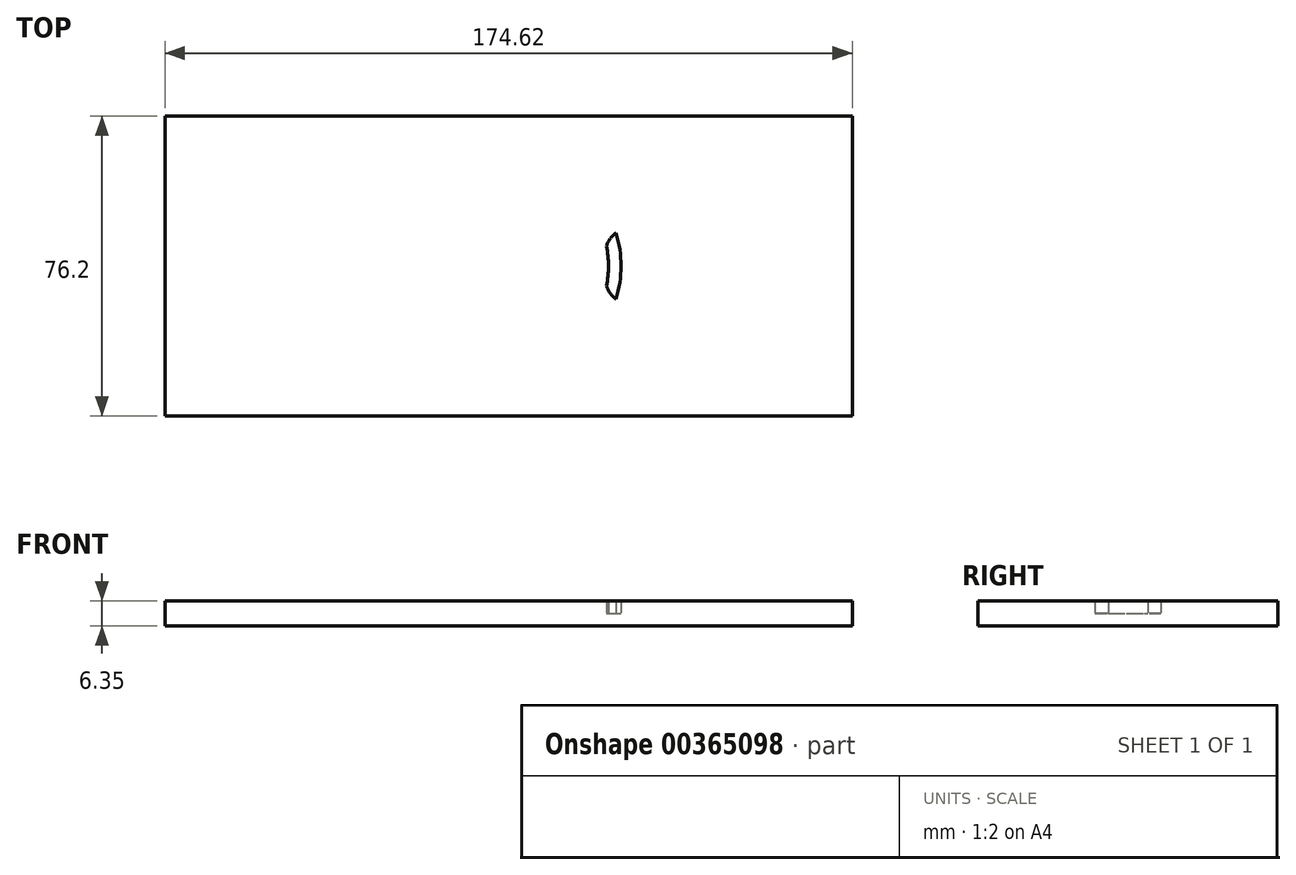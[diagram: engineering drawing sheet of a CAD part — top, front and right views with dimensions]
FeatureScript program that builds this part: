
annotation { "Feature Type Name" : "Feature", "Feature Type Description" : "" }
export const myFeature = defineFeature(function(context is Context, id is Id, definition is map)
    precondition{}
    {
        {
            var Q0;
            Q0=qCreatedBy(makeId("Top.planeOp"),FACE);
            var sketch = newSketch(context, id + "F0", { "sketchPlane" : qUnion([Q0])});
            skCircle(sketch, "E0", {"center": v(0, 0) * mm, "radius": 28.58 * mm});
            skLineSegment(sketch, "E1.bottom", {"start": v(87.31, -38.1) * mm, "end": v(-87.31, -38.1) * mm});
            skLineSegment(sketch, "E1.top", {"start": v(87.31, 38.1) * mm, "end": v(-87.31, 38.1) * mm});
            skLineSegment(sketch, "E1.left", {"start": v(87.31, -38.1) * mm, "end": v(87.31, 38.1) * mm});
            skLineSegment(sketch, "E1.right", {"start": v(-87.31, -38.1) * mm, "end": v(-87.31, 38.1) * mm});
            skLineSegment(sketch, "E2.bottom", {"start": v(25.4, -25.4) * mm, "end": v(-25.4, -25.4) * mm});
            skLineSegment(sketch, "E2.top", {"start": v(25.4, 25.4) * mm, "end": v(-25.4, 25.4) * mm});
            skLineSegment(sketch, "E2.left", {"start": v(25.4, -25.4) * mm, "end": v(25.4, 25.4) * mm});
            skLineSegment(sketch, "E2.right", {"start": v(-25.4, -25.4) * mm, "end": v(-25.4, 25.4) * mm});
            skCircle(sketch, "E3", {"center": v(-25.4, 25.4) * mm, "radius": 1.59 * mm});
            skCircle(sketch, "E4", {"center": v(-25.4, -25.4) * mm, "radius": 1.59 * mm});
            skCircle(sketch, "E5", {"center": v(25.4, -25.4) * mm, "radius": 1.59 * mm});
            skCircle(sketch, "E6", {"center": v(25.4, 25.4) * mm, "radius": 1.59 * mm});
            skCircle(sketch, "E7.0", {"center": v(0, 0) * mm, "radius": 25.4 * mm});
            skSolve(sketch);
        }
        {
            var Q0;
            Q0=makeQuery(id+"F0.imprint","IMPRINT",FACE,{"disambiguationData":[TD([[makeQuery(id+"F0.imprint","IMPRINT",EDGE,{"derivedFrom":sQuery(id+"F0.wireOp",EDGE,"E1.bottom")}),-1.0]])]});
            var Q1;
            {var subQ0=sQuery(id+"F0.wireOp",EDGE,"E2.left");var subQ1=sQuery(id+"F0.wireOp",EDGE,"E0");var subQ2=makeQuery(id+"F0.imprint","INTERSECT",VERTEX,{"derivedFrom":[subQ1,subQ0]});Q1=makeQuery(id+"F0.imprint","IMPRINT",FACE,{"disambiguationData":[TD([[makeQuery(id+"F0.imprint","IMPRINT",EDGE,{"disambiguationData":[TD([[subQ2,1.0]])],"derivedFrom":subQ1}),-1.0]])]});}
            var Q2;
            {var subQ0=sQuery(id+"F0.wireOp",EDGE,"E2.right");var subQ1=sQuery(id+"F0.wireOp",EDGE,"E0");var subQ2=makeQuery(id+"F0.imprint","INTERSECT",VERTEX,{"derivedFrom":[subQ1,subQ0]});Q2=makeQuery(id+"F0.imprint","IMPRINT",FACE,{"disambiguationData":[TD([[makeQuery(id+"F0.imprint","IMPRINT",EDGE,{"disambiguationData":[TD([[subQ2,-1.0]])],"derivedFrom":subQ1}),-1.0]])]});}
            var Q3;
            {var subQ0=sQuery(id+"F0.wireOp",EDGE,"E2.top");var subQ1=sQuery(id+"F0.wireOp",EDGE,"E0");var subQ2=makeQuery(id+"F0.imprint","INTERSECT",VERTEX,{"derivedFrom":[subQ1,subQ0]});Q3=makeQuery(id+"F0.imprint","IMPRINT",FACE,{"disambiguationData":[TD([[makeQuery(id+"F0.imprint","IMPRINT",EDGE,{"disambiguationData":[TD([[subQ2,1.0]])],"derivedFrom":subQ1}),-1.0]])]});}
            var Q4;
            {var subQ0=sQuery(id+"F0.wireOp",EDGE,"E2.top");var subQ1=sQuery(id+"F0.wireOp",EDGE,"E0");var subQ2=makeQuery(id+"F0.imprint","INTERSECT",VERTEX,{"derivedFrom":[subQ1,subQ0]});Q4=makeQuery(id+"F0.imprint","IMPRINT",FACE,{"disambiguationData":[TD([[makeQuery(id+"F0.imprint","IMPRINT",EDGE,{"disambiguationData":[TD([[subQ2,-1.0]])],"derivedFrom":subQ1}),-1.0]])]});}
            var Q5;
            {var subQ0=sQuery(id+"F0.wireOp",EDGE,"E7.0");var subQ1=makeQuery(id+"F0.imprint","INTERSECT",VERTEX,{"derivedFrom":[sQuery(id+"F0.wireOp",EDGE,"E2.top"),subQ0]});Q5=makeQuery(id+"F0.imprint","IMPRINT",FACE,{"disambiguationData":[TD([[makeQuery(id+"F0.imprint","IMPRINT",EDGE,{"disambiguationData":[TD([[subQ1,1.0]])],"derivedFrom":subQ0}),1.0]])]});}
            extrude(context, id + "F1", {"entities" : qUnion([Q0, Q1, Q2, Q3, Q4, Q5]), "depth" : 6.35 * mm});
        }
        {
            var Q0;
            Q0=qCreatedBy(makeId("Top.planeOp"),FACE);
            var sketch = newSketch(context, id + "F2", { "sketchPlane" : qUnion([Q0])});
            skLineSegment(sketch, "E8.0", {"start": v(87.31, -38.1) * mm, "end": v(-87.31, -38.1) * mm});
            skLineSegment(sketch, "E9.0", {"start": v(-87.31, -38.1) * mm, "end": v(-87.31, 38.1) * mm});
            skLineSegment(sketch, "E10.0", {"start": v(87.31, 38.1) * mm, "end": v(-87.31, 38.1) * mm});
            skLineSegment(sketch, "E11.0.0", {"start": v(87.31, -38.1) * mm, "end": v(87.31, 38.1) * mm});
            skLineSegment(sketch, "E11.0.2", {"start": v(-87.31, 38.1) * mm, "end": v(-87.31, -38.1) * mm});
            skLineSegment(sketch, "E11.0.3", {"start": v(-87.31, -38.1) * mm, "end": v(87.31, -38.1) * mm});
            skLineSegment(sketch, "E12.bottom", {"start": v(56.36, -9.53) * mm, "end": v(30.96, -9.52) * mm});
            skLineSegment(sketch, "E12.top", {"start": v(56.36, 9.53) * mm, "end": v(30.96, 9.53) * mm});
            skLineSegment(sketch, "E12.left", {"start": v(62.7, -3.18) * mm, "end": v(62.7, 3.18) * mm});
            skLineSegment(sketch, "E12.right", {"start": v(24.6, -3.17) * mm, "end": v(24.6, 3.18) * mm});
            skPoint(sketch, "E12.middle", {"position": v(43.66, 0) * mm});
            skLineSegment(sketch, "E13", {"start": v(0, 0) * mm, "end": v(43.66, 0) * mm});
            skLineSegment(sketch, "E14", {"start": v(43.66, 0) * mm, "end": v(87.31, 0) * mm});
            skPoint(sketch, "E15.visualSharp", {"position": v(24.6, 9.53) * mm});
            skArc(sketch, "E15.filletArc", {"start": v(30.96, 9.53) * mm, "mid": v(26.47, 7.67) * mm, "end": v(24.6, 3.18) * mm});
            skPoint(sketch, "E16.visualSharp", {"position": v(62.7, 9.53) * mm});
            skArc(sketch, "E16.filletArc", {"start": v(62.7, 3.18) * mm, "mid": v(60.85, 7.67) * mm, "end": v(56.36, 9.53) * mm});
            skPoint(sketch, "E17.visualSharp", {"position": v(62.7, -9.53) * mm});
            skArc(sketch, "E17.filletArc", {"start": v(56.36, -9.53) * mm, "mid": v(60.85, -7.67) * mm, "end": v(62.7, -3.18) * mm});
            skPoint(sketch, "E18.visualSharp", {"position": v(24.6, -9.52) * mm});
            skArc(sketch, "E18.filletArc", {"start": v(24.6, -3.17) * mm, "mid": v(26.47, -7.67) * mm, "end": v(30.96, -9.52) * mm});
            skLineSegment(sketch, "E19.bottom", {"start": v(37.3, -5.71) * mm, "end": v(50, -5.71) * mm});
            skLineSegment(sketch, "E19.top", {"start": v(37.3, 5.72) * mm, "end": v(50, 5.72) * mm});
            skLineSegment(sketch, "E19.left", {"start": v(37.3, -5.71) * mm, "end": v(37.3, 5.72) * mm});
            skLineSegment(sketch, "E19.right", {"start": v(50, -5.71) * mm, "end": v(50, 5.72) * mm});
            skLineSegment(sketch, "E20", {"start": v(30.32, 0) * mm, "end": v(57, 0) * mm});
            skCircle(sketch, "E21", {"center": v(30.32, 0) * mm, "radius": 1.59 * mm});
            skCircle(sketch, "E22", {"center": v(57, 0) * mm, "radius": 1.59 * mm});
            skLineSegment(sketch, "E23.MirrorCS", {"start": v(0, 0) * mm, "end": v(-43.66, 0) * mm});
            skLineSegment(sketch, "E24.bottom", {"start": v(-30, -9.52) * mm, "end": v(-57.3, -9.53) * mm});
            skLineSegment(sketch, "E24.top", {"start": v(-30, 9.53) * mm, "end": v(-57.3, 9.53) * mm});
            skLineSegment(sketch, "E24.left", {"start": v(-30, -9.52) * mm, "end": v(-30, 9.53) * mm});
            skLineSegment(sketch, "E24.right", {"start": v(-57.3, -9.52) * mm, "end": v(-57.3, 9.53) * mm});
            skPoint(sketch, "E24.middle", {"position": v(-43.66, 0) * mm});
            skLineSegment(sketch, "E25", {"start": v(-63.66, 0) * mm, "end": v(-23.65, 0) * mm});
            skCircle(sketch, "E26", {"center": v(-63.66, 0) * mm, "radius": 1.59 * mm});
            skCircle(sketch, "E27", {"center": v(-23.65, 0) * mm, "radius": 1.59 * mm});
            skSolve(sketch);
        }
        {
            var Q0;
            {var subQ13=sQuery(id+"F2.wireOp",EDGE,"E10.0");Q0=makeQuery(id+"F2.imprint","IMPRINT",FACE,{"disambiguationData":[TD([[makeQuery(id+"F2.imprint","IMPRINT",EDGE,{"derivedFrom":subQ13}),1.0]])]});}
            extrude(context, id + "F3", {"entities" : qUnion([Q0]), "depth" : 6.35 * mm});
        }
        {
            var Q0;
            Q0=makeQuery(id+"F2.imprint","IMPRINT",FACE,{"disambiguationData":[TD([[makeQuery(id+"F2.imprint","IMPRINT",EDGE,{"derivedFrom":sQuery(id+"F2.wireOp",EDGE,"E12.bottom")}),-1.0]])]});
            var Q1;
            Q1=makeQuery(id+"F2.imprint","IMPRINT",FACE,{"disambiguationData":[TD([[makeQuery(id+"F2.imprint","IMPRINT",EDGE,{"derivedFrom":sQuery(id+"F2.wireOp",EDGE,"E12.top")}),1.0]])]});
            extrude(context, id + "F4", {"entities" : qUnion([Q0, Q1]), "operationType" : NewBodyOperationType.ADD, "depth" : 3.17 * mm});
        }
    });
